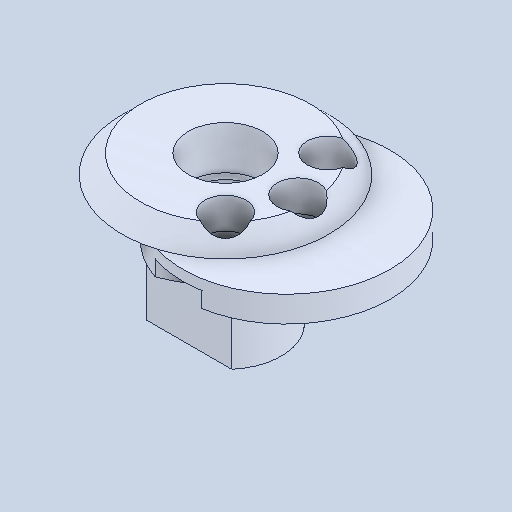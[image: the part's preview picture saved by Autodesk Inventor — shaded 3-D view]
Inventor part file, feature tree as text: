
AUTODESK INVENTOR PART (.ipt)
format: ipt  version: 2024 (Build 280153000, 153)  size: 159,232 bytes
history: native  units: in
note: dims shown in document units (in); Inventor stores cm internally (conversion verified against a paired STEP export)
features: fillet x1
ambient origin geometry x8: Origin, YZ Plane, XZ Plane, XY Plane, X Axis, Y Axis, Z Axis, Center Point
bodies: Solid1 (feature_tree)
feature tree (1):
  fillet  "FILLET1"  [1 undecoded]
note: 1 required parameter value undecoded (feature->parameter linkage not recoverable at this tier; creation-order binding heuristic only, values carry confidence <= 0.55)
